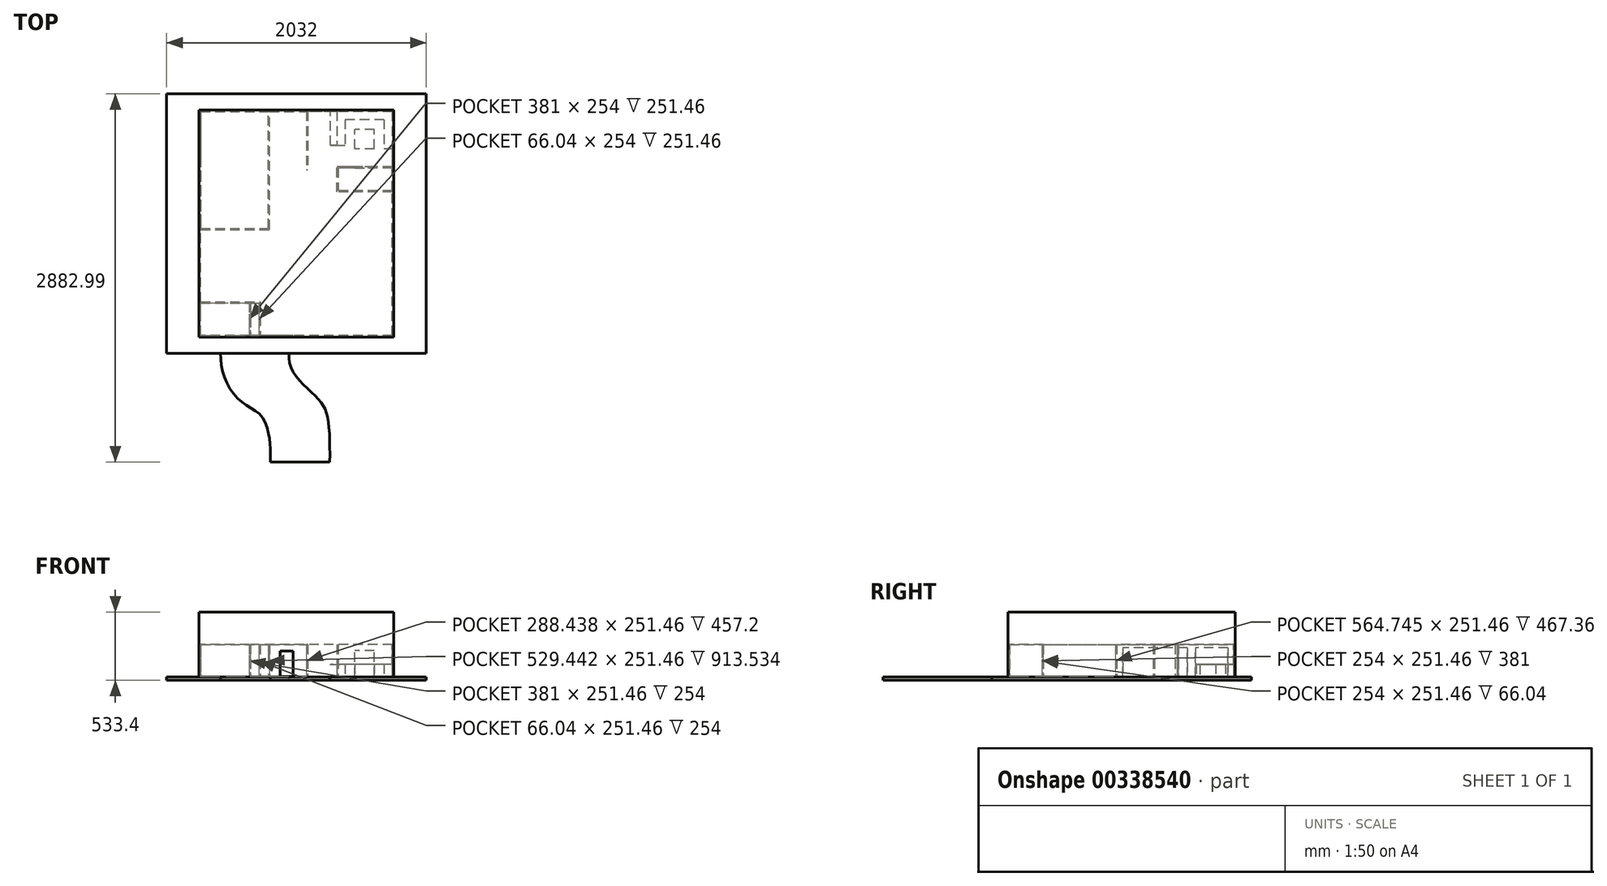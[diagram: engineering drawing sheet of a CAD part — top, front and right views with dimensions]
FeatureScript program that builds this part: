
annotation { "Feature Type Name" : "Feature", "Feature Type Description" : "" }
export const myFeature = defineFeature(function(context is Context, id is Id, definition is map)
    precondition{}
    {
        {
            var Q0;
            Q0=qCreatedBy(makeId("Top.planeOp"),FACE);
            var sketch = newSketch(context, id + "F0", { "sketchPlane" : qUnion([Q0])});
            skLineSegment(sketch, "E0.bottom", {"start": v(1016, 1016) * mm, "end": v(-1016, 1016) * mm});
            skLineSegment(sketch, "E0.top", {"start": v(1016, -1016) * mm, "end": v(-1016, -1016) * mm});
            skLineSegment(sketch, "E0.left", {"start": v(1016, 1016) * mm, "end": v(1016, -1016) * mm});
            skLineSegment(sketch, "E0.right", {"start": v(-1016, 1016) * mm, "end": v(-1016, -1016) * mm});
            skPoint(sketch, "E0.middle", {"position": v(0, 0) * mm});
            skSolve(sketch);
        }
        {
            var Q0;
            Q0 = qSketchRegion(id + "F0", true);
            extrude(context, id + "F1", {"entities" : qUnion([Q0]), "depth" : 25.4 * mm});
        }
        {
            var Q0;
            Q0=makeQuery(id+"F1.opExtrude","CAP_FACE",FACE,{"disambiguationData":[OSD([sQuery(id+"F0.wireOp",EDGE,"E0.bottom"),sQuery(id+"F0.wireOp",EDGE,"E0.top"),sQuery(id+"F0.wireOp",EDGE,"E0.left"),sQuery(id+"F0.wireOp",EDGE,"E0.right")])],"isStart":false});
            var sketch = newSketch(context, id + "F2", { "sketchPlane" : qUnion([Q0])});
            skLineSegment(sketch, "E1.bottom", {"start": v(762, -889) * mm, "end": v(-762, -889) * mm});
            skLineSegment(sketch, "E1.top", {"start": v(762, 889) * mm, "end": v(-762, 889) * mm});
            skLineSegment(sketch, "E1.left", {"start": v(762, -889) * mm, "end": v(762, 889) * mm});
            skLineSegment(sketch, "E1.right", {"start": v(-762, -889) * mm, "end": v(-762, 889) * mm});
            skPoint(sketch, "E1.middle", {"position": v(0, 0) * mm});
            skSolve(sketch);
        }
        {
            var Q0;
            Q0 = qSketchRegion(id + "F2", true);
            extrude(context, id + "F3", {"entities" : qUnion([Q0]), "depth" : 254 * mm});
        }
        {
            var Q0;
            Q0=makeQuery(id+"F3.opExtrude","CAP_FACE",FACE,{"disambiguationData":[OSD([sQuery(id+"F2.wireOp",EDGE,"E1.bottom"),sQuery(id+"F2.wireOp",EDGE,"E1.top"),sQuery(id+"F2.wireOp",EDGE,"E1.left"),sQuery(id+"F2.wireOp",EDGE,"E1.right")])],"isStart":false});
            var sketch = newSketch(context, id + "F4", { "sketchPlane" : qUnion([Q0])});
            skLineSegment(sketch, "E2.bottom", {"start": v(762, 889) * mm, "end": v(-762, 889) * mm});
            skLineSegment(sketch, "E2.top", {"start": v(762, -889) * mm, "end": v(-762, -889) * mm});
            skLineSegment(sketch, "E2.left", {"start": v(762, 889) * mm, "end": v(762, -889) * mm});
            skLineSegment(sketch, "E2.right", {"start": v(-762, 889) * mm, "end": v(-762, -889) * mm});
            skPoint(sketch, "E2.middle", {"position": v(0, 0) * mm});
            skSolve(sketch);
        }
        {
            var Q0;
            Q0 = qSketchRegion(id + "F4", true);
            extrude(context, id + "F5", {"entities" : qUnion([Q0]), "depth" : 254 * mm});
        }
        {
            var Q0;
            Q0=makeQuery(id+"F3.opExtrude","CAP_FACE",FACE,{"disambiguationData":[OSD([sQuery(id+"F2.wireOp",EDGE,"E1.bottom"),sQuery(id+"F2.wireOp",EDGE,"E1.top"),sQuery(id+"F2.wireOp",EDGE,"E1.left"),sQuery(id+"F2.wireOp",EDGE,"E1.right")])],"isStart":false});
            var sketch = newSketch(context, id + "F6", { "sketchPlane" : qUnion([Q0])});
            skLineSegment(sketch, "E3.bottom", {"start": v(749.3, 876.3) * mm, "end": v(-749.3, 876.3) * mm});
            skLineSegment(sketch, "E3.top", {"start": v(749.3, -876.3) * mm, "end": v(-749.3, -876.3) * mm});
            skLineSegment(sketch, "E3.left", {"start": v(749.3, 876.3) * mm, "end": v(749.3, -876.3) * mm});
            skLineSegment(sketch, "E3.right", {"start": v(-749.3, 876.3) * mm, "end": v(-749.3, -876.3) * mm});
            skPoint(sketch, "E3.middle", {"position": v(0, 0) * mm});
            skSolve(sketch);
        }
        {
            var Q0;
            Q0 = qSketchRegion(id + "F6", true);
            extrude(context, id + "F7", {"entities" : qUnion([Q0]), "operationType" : NewBodyOperationType.REMOVE, "oppositeDirection" : true, "depth" : 251.46 * mm});
        }
        {
            var Q0;
            Q0=makeQuery(id+"F1.opExtrude","CAP_FACE",FACE,{"disambiguationData":[OSD([sQuery(id+"F0.wireOp",EDGE,"E0.bottom"),sQuery(id+"F0.wireOp",EDGE,"E0.top"),sQuery(id+"F0.wireOp",EDGE,"E0.left"),sQuery(id+"F0.wireOp",EDGE,"E0.right")])],"isStart":false});
            var sketch = newSketch(context, id + "F8", { "sketchPlane" : qUnion([Q0])});
            skFitSpline(sketch, "E4", {"points": [v(-584.93, -891.55) * mm, v(-580.5, -1148.7) * mm, v(-438.6, -1388.14) * mm, v(-274.56, -1507.85) * mm, v(-208.05, -1711.8) * mm, v(-203.61, -1867) * mm], "startDerivative": vector(-115.09, -1178.52) * mm, "endDerivative": vector(-14.83, -861.47) * mm});
            skFitSpline(sketch, "E5", {"points": [v(-39.56, -891.55) * mm, v(-39.56, -1135.4) * mm, v(159.96, -1361.53) * mm, v(244.2, -1521.15) * mm, v(257.5, -2013.31) * mm], "startDerivative": vector(-223.74, -1101.06) * mm, "endDerivative": vector(-42.26, -1754.4) * mm});
            skLineSegment(sketch, "E6", {"start": v(-203.61, -1867) * mm, "end": v(262.06, -1867) * mm});
            skLineSegment(sketch, "E7", {"start": v(-584.93, -891.55) * mm, "end": v(-39.56, -891.55) * mm});
            skPoint(sketch, "E8.start.orphan", {"position": v(-670.54, -1388.14) * mm});
            skSolve(sketch);
        }
        {
            var Q0;
            {var subQ0=sQuery(id+"F8.wireOp",EDGE,"E6");var subQ1=sQuery(id+"F8.wireOp",EDGE,"E4");var subQ2=makeQuery(id+"F8.imprint","INTERSECT",VERTEX,{"derivedFrom":[subQ1,subQ0]});Q0=makeQuery(id+"F8.imprint","IMPRINT",FACE,{"disambiguationData":[TD([[makeQuery(id+"F8.imprint","IMPRINT",EDGE,{"disambiguationData":[TD([[subQ2,1.0]])],"derivedFrom":subQ1}),1.0]])]});}
            extrude(context, id + "F9", {"entities" : qUnion([Q0]), "oppositeDirection" : true, "depth" : 25.4 * mm});
        }
        {
            var Q0;
            Q0=makeQuery(id+"F3.opExtrude","SWEPT_FACE",FACE,{"disambiguationData":[OSD([sQuery(id+"F2.wireOp",EDGE,"E1.right")])]});
            var sketch = newSketch(context, id + "F10", { "sketchPlane" : qUnion([Q0])});
            skLineSegment(sketch, "E9.bottom", {"start": v(-833.77, 25.4) * mm, "end": v(-579.77, 25.4) * mm});
            skLineSegment(sketch, "E9.top", {"start": v(-833.77, 254) * mm, "end": v(-579.77, 254) * mm});
            skLineSegment(sketch, "E9.left", {"start": v(-833.77, 25.4) * mm, "end": v(-833.77, 254) * mm});
            skLineSegment(sketch, "E9.right", {"start": v(-579.77, 25.4) * mm, "end": v(-579.77, 254) * mm});
            skLineSegment(sketch, "E10.bottom", {"start": v(-516.27, 25.4) * mm, "end": v(-8.27, 25.4) * mm});
            skLineSegment(sketch, "E10.top", {"start": v(-516.27, 254) * mm, "end": v(-8.27, 254) * mm});
            skLineSegment(sketch, "E10.left", {"start": v(-516.27, 25.4) * mm, "end": v(-516.27, 254) * mm});
            skLineSegment(sketch, "E10.right", {"start": v(-8.27, 25.4) * mm, "end": v(-8.27, 254) * mm});
            skSolve(sketch);
        }
        {
            var Q0;
            Q0=makeQuery(id+"F10.imprint","IMPRINT",FACE,{"disambiguationData":[TD([[makeQuery(id+"F10.imprint","IMPRINT",EDGE,{"derivedFrom":sQuery(id+"F10.wireOp",EDGE,"E9.bottom")}),-1.0]])]});
            var Q1;
            Q1=makeQuery(id+"F10.imprint","IMPRINT",FACE,{"disambiguationData":[TD([[makeQuery(id+"F10.imprint","IMPRINT",EDGE,{"derivedFrom":sQuery(id+"F10.wireOp",EDGE,"E10.bottom")}),-1.0]])]});
            var Q2;
            Q2=makeQuery(id+"F7.boolean.opBoolean","COPY",FACE,{"derivedFrom":makeQuery(id+"F7.opExtrude","SWEPT_FACE",FACE,{"disambiguationData":[OSD([sQuery(id+"F6.wireOp",EDGE,"E3.right")])]})});
            extrude(context, id + "F11", {"entities" : qUnion([Q0, Q1]), "operationType" : NewBodyOperationType.REMOVE, "endBound" : BoundingType.UP_TO_SURFACE, "oppositeDirection" : true, "endBoundEntityFace" : qUnion([Q2]), "depth" : 25.4 * mm});
        }
        {
            var Q0;
            Q0=makeQuery(id+"F7.boolean.opBoolean","COPY",FACE,{"derivedFrom":makeQuery(id+"F7.opExtrude","CAP_FACE",FACE,{"disambiguationData":[OSD([sQuery(id+"F6.wireOp",EDGE,"E3.bottom"),sQuery(id+"F6.wireOp",EDGE,"E3.top"),sQuery(id+"F6.wireOp",EDGE,"E3.left"),sQuery(id+"F6.wireOp",EDGE,"E3.right")])],"isStart":false})});
            var sketch = newSketch(context, id + "F12", { "sketchPlane" : qUnion([Q0])});
            skLineSegment(sketch, "E11.bottom", {"start": v(-749.3, -47.4) * mm, "end": v(-209.7, -47.4) * mm});
            skLineSegment(sketch, "E11.top", {"start": v(-749.3, -37.23) * mm, "end": v(-219.86, -37.23) * mm});
            skLineSegment(sketch, "E11.left", {"start": v(-749.3, -47.4) * mm, "end": v(-749.3, -37.23) * mm});
            skLineSegment(sketch, "E11.right", {"start": v(-209.7, -47.4) * mm, "end": v(-209.7, -37.23) * mm});
            skLineSegment(sketch, "E12.bottom", {"start": v(-209.7, -47.4) * mm, "end": v(-219.86, -47.4) * mm});
            skLineSegment(sketch, "E12.top", {"start": v(-209.7, 876.3) * mm, "end": v(-219.86, 876.3) * mm});
            skLineSegment(sketch, "E12.left", {"start": v(-209.7, -47.4) * mm, "end": v(-209.7, 876.3) * mm});
            skLineSegment(sketch, "E12.right", {"start": v(-219.86, -37.23) * mm, "end": v(-219.86, 876.3) * mm});
            skLineSegment(sketch, "E13.bottom", {"start": v(-749.3, -612.14) * mm, "end": v(-358.14, -612.14) * mm});
            skLineSegment(sketch, "E13.top", {"start": v(-749.3, -622.3) * mm, "end": v(-368.3, -622.3) * mm});
            skLineSegment(sketch, "E13.left", {"start": v(-749.3, -612.14) * mm, "end": v(-749.3, -622.3) * mm});
            skLineSegment(sketch, "E14.bottom", {"start": v(-358.14, -612.14) * mm, "end": v(-368.3, -612.14) * mm});
            skLineSegment(sketch, "E14.top", {"start": v(-358.14, -876.3) * mm, "end": v(-368.3, -876.3) * mm});
            skLineSegment(sketch, "E14.left", {"start": v(-358.14, -622.3) * mm, "end": v(-358.14, -876.3) * mm});
            skLineSegment(sketch, "E14.right", {"start": v(-368.3, -622.3) * mm, "end": v(-368.3, -876.3) * mm});
            skLineSegment(sketch, "E15.bottom", {"start": v(-358.14, -612.14) * mm, "end": v(-281.94, -612.14) * mm});
            skLineSegment(sketch, "E15.top", {"start": v(-358.14, -622.3) * mm, "end": v(-292.1, -622.3) * mm});
            skLineSegment(sketch, "E15.right", {"start": v(-281.94, -612.14) * mm, "end": v(-281.94, -622.3) * mm});
            skLineSegment(sketch, "E16.top", {"start": v(-281.94, -876.3) * mm, "end": v(-292.1, -876.3) * mm});
            skLineSegment(sketch, "E16.left", {"start": v(-281.94, -622.3) * mm, "end": v(-281.94, -876.3) * mm});
            skLineSegment(sketch, "E16.right", {"start": v(-292.1, -622.3) * mm, "end": v(-292.1, -876.3) * mm});
            skLineSegment(sketch, "E17.bottom", {"start": v(88.9, 876.3) * mm, "end": v(78.74, 876.3) * mm});
            skLineSegment(sketch, "E17.top", {"start": v(88.9, 419.1) * mm, "end": v(78.74, 419.1) * mm});
            skLineSegment(sketch, "E17.left", {"start": v(88.9, 876.3) * mm, "end": v(88.9, 419.1) * mm});
            skLineSegment(sketch, "E17.right", {"start": v(78.74, 876.3) * mm, "end": v(78.74, 419.1) * mm});
            skLineSegment(sketch, "E18.bottom", {"start": v(749.3, 256.54) * mm, "end": v(327.66, 256.54) * mm});
            skLineSegment(sketch, "E18.top", {"start": v(749.3, 246.38) * mm, "end": v(317.5, 246.38) * mm});
            skLineSegment(sketch, "E18.left", {"start": v(749.3, 256.54) * mm, "end": v(749.3, 246.38) * mm});
            skLineSegment(sketch, "E19.bottom", {"start": v(749.3, 434.34) * mm, "end": v(327.66, 434.34) * mm});
            skLineSegment(sketch, "E19.top", {"start": v(749.3, 444.5) * mm, "end": v(317.5, 444.5) * mm});
            skLineSegment(sketch, "E19.left", {"start": v(749.3, 434.34) * mm, "end": v(749.3, 444.5) * mm});
            skLineSegment(sketch, "E19.right", {"start": v(317.5, 434.34) * mm, "end": v(317.5, 444.5) * mm});
            skLineSegment(sketch, "E20.bottom", {"start": v(317.5, 444.5) * mm, "end": v(520.7, 444.5) * mm});
            skLineSegment(sketch, "E20.top", {"start": v(327.66, 256.54) * mm, "end": v(520.7, 256.54) * mm});
            skLineSegment(sketch, "E20.left", {"start": v(317.5, 444.5) * mm, "end": v(317.5, 256.54) * mm});
            skLineSegment(sketch, "E21", {"start": v(327.66, 434.34) * mm, "end": v(327.66, 256.54) * mm});
            skLineSegment(sketch, "E22", {"start": v(317.5, 256.54) * mm, "end": v(317.5, 246.38) * mm});
            skPoint(sketch, "E18.right.start.orphan", {"position": v(292.1, 256.54) * mm});
            skSolve(sketch);
        }
        {
            var Q0;
            Q0=makeQuery(id+"F12.imprint","IMPRINT",FACE,{"disambiguationData":[TD([[makeQuery(id+"F12.imprint","IMPRINT",EDGE,{"derivedFrom":sQuery(id+"F12.wireOp",EDGE,"E11.bottom")}),1.0]])]});
            var Q1;
            Q1=makeQuery(id+"F12.imprint","IMPRINT",FACE,{"disambiguationData":[TD([[makeQuery(id+"F12.imprint","IMPRINT",EDGE,{"derivedFrom":sQuery(id+"F12.wireOp",EDGE,"E13.bottom")}),-1.0]])]});
            var Q2;
            Q2=makeQuery(id+"F12.imprint","IMPRINT",FACE,{"disambiguationData":[TD([[makeQuery(id+"F12.imprint","IMPRINT",EDGE,{"derivedFrom":sQuery(id+"F12.wireOp",EDGE,"E17.bottom")}),1.0]])]});
            var Q3;
            Q3=makeQuery(id+"F12.imprint","IMPRINT",FACE,{"disambiguationData":[TD([[makeQuery(id+"F12.imprint","IMPRINT",EDGE,{"derivedFrom":sQuery(id+"F12.wireOp",EDGE,"E18.bottom")}),1.0]])]});
            var Q4;
            Q4=makeQuery(id+"F12.imprint","IMPRINT",FACE,{"disambiguationData":[TD([[makeQuery(id+"F12.imprint","IMPRINT",EDGE,{"derivedFrom":sQuery(id+"F12.wireOp",EDGE,"E19.bottom")}),-1.0]])]});
            extrude(context, id + "F13", {"entities" : qUnion([Q0, Q1, Q2, Q3, Q4]), "operationType" : NewBodyOperationType.ADD, "endBound" : BoundingType.UP_TO_NEXT, "depth" : 25.4 * mm});
        }
        {
            var Q0;
            Q0=makeQuery(id+"F3.opExtrude","SWEPT_FACE",FACE,{"disambiguationData":[OSD([sQuery(id+"F2.wireOp",EDGE,"E1.bottom")])]});
            var sketch = newSketch(context, id + "F14", { "sketchPlane" : qUnion([Q0])});
            skLineSegment(sketch, "E23.bottom", {"start": v(-25.4, 25.4) * mm, "end": v(-127, 25.4) * mm});
            skLineSegment(sketch, "E23.top", {"start": v(-25.4, 228.6) * mm, "end": v(-127, 228.6) * mm});
            skLineSegment(sketch, "E23.left", {"start": v(-25.4, 25.4) * mm, "end": v(-25.4, 228.6) * mm});
            skLineSegment(sketch, "E23.right", {"start": v(-127, 25.4) * mm, "end": v(-127, 228.6) * mm});
            skSolve(sketch);
        }
        {
            var Q0;
            Q0=makeQuery(id+"F14.imprint","IMPRINT",FACE,{"disambiguationData":[TD([[makeQuery(id+"F14.imprint","IMPRINT",EDGE,{"derivedFrom":sQuery(id+"F14.wireOp",EDGE,"E23.bottom")}),-1.0]])]});
            var Q1;
            {var subQ0=sQuery(id+"F6.wireOp",EDGE,"E3.left");var subQ5=sQuery(id+"F6.wireOp",EDGE,"E3.top");Q1=makeQuery(id+"F13.boolean.opBoolean","SPLIT",FACE,{"disambiguationData":[TD([makeQuery(id+"F7.boolean.opBoolean","COPY",FACE,{"derivedFrom":makeQuery(id+"F7.opExtrude","SWEPT_FACE",FACE,{"disambiguationData":[OSD([subQ0])]})})])],"derivedFrom":makeQuery(id+"F7.boolean.opBoolean","COPY",FACE,{"derivedFrom":makeQuery(id+"F7.opExtrude","SWEPT_FACE",FACE,{"disambiguationData":[OSD([subQ5])]})})});}
            extrude(context, id + "F15", {"entities" : qUnion([Q0]), "operationType" : NewBodyOperationType.REMOVE, "endBound" : BoundingType.UP_TO_SURFACE, "oppositeDirection" : true, "endBoundEntityFace" : qUnion([Q1]), "depth" : 25.4 * mm});
        }
        {
            var Q0;
            {var subQ0=sQuery(id+"F6.wireOp",EDGE,"E3.left");var subQ1=sQuery(id+"F6.wireOp",EDGE,"E3.bottom");var subQ2=sQuery(id+"F6.wireOp",EDGE,"E3.top");var subQ3=sQuery(id+"F6.wireOp",EDGE,"E3.right");Q0=makeQuery(id+"F13.boolean.opBoolean","SPLIT",FACE,{"disambiguationData":[TD([makeQuery(id+"F7.boolean.opBoolean","COPY",FACE,{"derivedFrom":makeQuery(id+"F7.opExtrude","SWEPT_FACE",FACE,{"disambiguationData":[OSD([subQ0])]})})])],"derivedFrom":makeQuery(id+"F7.boolean.opBoolean","COPY",FACE,{"derivedFrom":makeQuery(id+"F7.opExtrude","CAP_FACE",FACE,{"disambiguationData":[OSD([subQ1,subQ2,subQ0,subQ3])],"isStart":false})})});}
            var sketch = newSketch(context, id + "F16", { "sketchPlane" : qUnion([Q0])});
            skLineSegment(sketch, "E24.bottom", {"start": v(609.6, 584.2) * mm, "end": v(457.2, 584.2) * mm});
            skLineSegment(sketch, "E24.top", {"start": v(609.6, 736.6) * mm, "end": v(457.2, 736.6) * mm});
            skLineSegment(sketch, "E24.left", {"start": v(609.6, 584.2) * mm, "end": v(609.6, 736.6) * mm});
            skLineSegment(sketch, "E24.right", {"start": v(457.2, 584.2) * mm, "end": v(457.2, 736.6) * mm});
            skPoint(sketch, "E24.middle", {"position": v(533.4, 660.4) * mm});
            skLineSegment(sketch, "E25.bottom", {"start": v(749.3, 876.3) * mm, "end": v(317.5, 876.3) * mm});
            skLineSegment(sketch, "E25.top", {"start": v(685.8, 812.8) * mm, "end": v(381, 812.8) * mm});
            skLineSegment(sketch, "E25.left", {"start": v(749.3, 876.3) * mm, "end": v(749.3, 812.8) * mm});
            skLineSegment(sketch, "E25.right", {"start": v(317.5, 876.3) * mm, "end": v(317.5, 812.8) * mm});
            skLineSegment(sketch, "E26.bottom", {"start": v(749.3, 876.3) * mm, "end": v(685.8, 876.3) * mm});
            skLineSegment(sketch, "E26.top", {"start": v(749.3, 584.2) * mm, "end": v(685.8, 584.2) * mm});
            skLineSegment(sketch, "E26.left", {"start": v(749.3, 876.3) * mm, "end": v(749.3, 584.2) * mm});
            skLineSegment(sketch, "E26.right", {"start": v(685.8, 812.8) * mm, "end": v(685.8, 584.2) * mm});
            skLineSegment(sketch, "E27.top", {"start": v(317.5, 611.97) * mm, "end": v(381, 611.97) * mm});
            skLineSegment(sketch, "E27.left", {"start": v(317.5, 812.8) * mm, "end": v(317.5, 611.97) * mm});
            skLineSegment(sketch, "E27.right", {"start": v(381, 812.8) * mm, "end": v(381, 611.97) * mm});
            skSolve(sketch);
        }
        {
            var Q0;
            Q0=makeQuery(id+"F16.imprint","IMPRINT",FACE,{"disambiguationData":[TD([[makeQuery(id+"F16.imprint","IMPRINT",EDGE,{"derivedFrom":sQuery(id+"F16.wireOp",EDGE,"E24.bottom")}),-1.0]])]});
            var Q1;
            Q1=makeQuery(id+"F16.imprint","IMPRINT",FACE,{"disambiguationData":[TD([[makeQuery(id+"F16.imprint","IMPRINT",EDGE,{"derivedFrom":sQuery(id+"F16.wireOp",EDGE,"E25.bottom")}),1.0]])]});
            extrude(context, id + "F17", {"entities" : qUnion([Q0, Q1]), "depth" : 96.52 * mm});
        }
        {
            var Q0;
            Q0=makeQuery(id+"F17.opExtrude","CAP_FACE",FACE,{"disambiguationData":[OSD([sQuery(id+"F16.wireOp",EDGE,"E25.bottom"),sQuery(id+"F16.wireOp",EDGE,"E25.top"),sQuery(id+"F16.wireOp",EDGE,"E25.right"),sQuery(id+"F16.wireOp",EDGE,"E26.bottom"),sQuery(id+"F16.wireOp",EDGE,"E26.top"),sQuery(id+"F16.wireOp",EDGE,"E26.left"),sQuery(id+"F16.wireOp",EDGE,"E26.right"),sQuery(id+"F16.wireOp",EDGE,"E27.top"),sQuery(id+"F16.wireOp",EDGE,"E27.left"),sQuery(id+"F16.wireOp",EDGE,"E27.right")])],"isStart":false});
            var sketch = newSketch(context, id + "F18", { "sketchPlane" : qUnion([Q0])});
            skLineSegment(sketch, "E28.bottom", {"start": v(325.72, 611.97) * mm, "end": v(266.7, 611.97) * mm});
            skLineSegment(sketch, "E28.top", {"start": v(325.72, 876.3) * mm, "end": v(266.7, 876.3) * mm});
            skLineSegment(sketch, "E28.left", {"start": v(325.72, 611.97) * mm, "end": v(325.72, 876.3) * mm});
            skLineSegment(sketch, "E28.right", {"start": v(266.7, 611.97) * mm, "end": v(266.7, 876.3) * mm});
            skSolve(sketch);
        }
        {
            var Q0;
            {var subQ2=sQuery(id+"F18.wireOp",EDGE,"E28.right");Q0=makeQuery(id+"F18.imprint","IMPRINT",FACE,{"disambiguationData":[TD([[makeQuery(id+"F18.imprint","IMPRINT",EDGE,{"derivedFrom":subQ2}),-1.0]])]});}
            extrude(context, id + "F19", {"entities" : qUnion([Q0]), "operationType" : NewBodyOperationType.ADD, "oppositeDirection" : true, "depth" : 5.08 * mm});
        }
        {
            var Q0;
            Q0=makeQuery(id+"F13.opExtrude","SWEPT_FACE",FACE,{"disambiguationData":[OSD([sQuery(id+"F12.wireOp",EDGE,"E19.top"),sQuery(id+"F12.wireOp",EDGE,"E20.bottom")])]});
            var sketch = newSketch(context, id + "F20", { "sketchPlane" : qUnion([Q0])});
            skLineSegment(sketch, "E29.bottom", {"start": v(-609.6, 27.94) * mm, "end": v(-457.2, 27.94) * mm});
            skLineSegment(sketch, "E29.top", {"start": v(-609.6, 231.14) * mm, "end": v(-457.2, 231.14) * mm});
            skLineSegment(sketch, "E29.left", {"start": v(-609.6, 27.94) * mm, "end": v(-609.6, 231.14) * mm});
            skLineSegment(sketch, "E29.right", {"start": v(-457.2, 27.94) * mm, "end": v(-457.2, 231.14) * mm});
            skSolve(sketch);
        }
        {
            var Q0;
            Q0=makeQuery(id+"F20.imprint","IMPRINT",FACE,{"disambiguationData":[TD([[makeQuery(id+"F20.imprint","IMPRINT",EDGE,{"derivedFrom":sQuery(id+"F20.wireOp",EDGE,"E29.bottom")}),1.0]])]});
            extrude(context, id + "F21", {"entities" : qUnion([Q0]), "operationType" : NewBodyOperationType.REMOVE, "oppositeDirection" : true, "depth" : 25.4 * mm});
        }
    });
